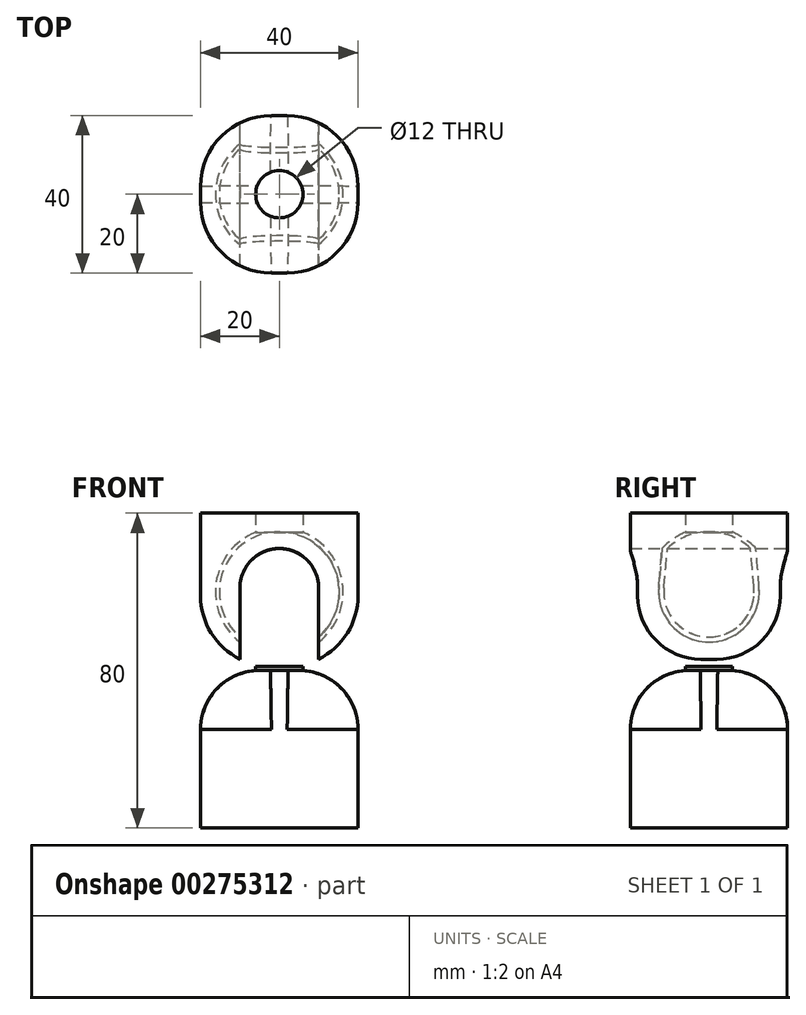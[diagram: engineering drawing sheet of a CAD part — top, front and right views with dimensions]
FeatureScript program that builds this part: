
annotation { "Feature Type Name" : "Feature", "Feature Type Description" : "" }
export const myFeature = defineFeature(function(context is Context, id is Id, definition is map)
    precondition{}
    {
        {
            var Q0;
            Q0=qCreatedBy(makeId("Front.planeOp"),FACE);
            var sketch = newSketch(context, id + "F0", { "sketchPlane" : qUnion([Q0])});
            skLineSegment(sketch, "E0.bottom", {"start": v(20, 20) * mm, "end": v(-20, 20) * mm});
            skLineSegment(sketch, "E0.top", {"start": v(20, -20) * mm, "end": v(-20, -20) * mm});
            skLineSegment(sketch, "E0.left", {"start": v(20, 20) * mm, "end": v(20, -20) * mm});
            skLineSegment(sketch, "E0.right", {"start": v(-20, 20) * mm, "end": v(-20, -20) * mm});
            skPoint(sketch, "E0.middle", {"position": v(0, 0) * mm});
            skSolve(sketch);
        }
        {
            var Q0;
            Q0 = qSketchRegion(id + "F0", true);
            extrude(context, id + "F1", {"entities" : qUnion([Q0]), "endBound" : BoundingType.SYMMETRIC, "depth" : 40 * mm});
        }
        {
            var Q0;
            Q0=qCreatedBy(makeId("Front.planeOp"),FACE);
            var sketch = newSketch(context, id + "F2", { "sketchPlane" : qUnion([Q0])});
            skLineSegment(sketch, "E1", {"start": v(0, 0) * mm, "end": v(0, 55.23) * mm});
            skArc(sketch, "E2", {"start": v(6, 26) * mm, "mid": v(14.92, 43.06) * mm, "end": v(0, 55.23) * mm});
            skLineSegment(sketch, "E3", {"start": v(6, 26) * mm, "end": v(6, 0) * mm});
            skLineSegment(sketch, "E4", {"start": v(6, 0) * mm, "end": v(0, 0) * mm});
            skSolve(sketch);
        }
        {
            var Q0;
            Q0=makeQuery(id+"F2.imprint","IMPRINT",FACE,{"disambiguationData":[TD([[makeQuery(id+"F2.imprint","IMPRINT",EDGE,{"derivedFrom":sQuery(id+"F2.wireOp",EDGE,"E1")}),-1.0]])]});
            var Q1;
            Q1=sQuery(id+"F2.wireOp",EDGE,"E1");
            revolve(context, id + "F3", {"operationType" : NewBodyOperationType.ADD, "entities" : qUnion([Q0]), "axis" : qUnion([Q1]), "revolveType" : RevolveType.FULL});
        }
        {
            var Q0;
            Q0=makeQuery(id+"F1.opExtrude","CAP_EDGE",EDGE,{"disambiguationData":[OSD([sQuery(id+"F0.wireOp",EDGE,"E0.left")])],"isStart":false});
            var Q1;
            Q1=makeQuery(id+"F1.opExtrude","CAP_EDGE",EDGE,{"disambiguationData":[OSD([sQuery(id+"F0.wireOp",EDGE,"E0.left")])],"isStart":true});
            var Q2;
            Q2=makeQuery(id+"F1.opExtrude","CAP_EDGE",EDGE,{"disambiguationData":[OSD([sQuery(id+"F0.wireOp",EDGE,"E0.right")])],"isStart":true});
            var Q3;
            Q3=makeQuery(id+"F1.opExtrude","CAP_EDGE",EDGE,{"disambiguationData":[OSD([sQuery(id+"F0.wireOp",EDGE,"E0.right")])],"isStart":false});
            fillet(context, id + "F4", {"entities" : qUnion([Q0, Q1, Q2, Q3]), "radius" : 18 * mm, "tangentPropagation" : true, "allowEdgeOverflow" : false});
        }
        {
            var Q0;
            Q0=makeQuery(id+"F1.opExtrude","SWEPT_FACE",FACE,{"disambiguationData":[OSD([sQuery(id+"F0.wireOp",EDGE,"E0.bottom")])]});
            var sketch = newSketch(context, id + "F5", { "sketchPlane" : qUnion([Q0])});
            skLineSegment(sketch, "E5.0.0", {"start": v(20, -2) * mm, "end": v(20, 2) * mm});
            skArc(sketch, "E5.0.1", {"start": v(20, 2) * mm, "mid": v(14.73, 14.73) * mm, "end": v(2, 20) * mm});
            skLineSegment(sketch, "E5.0.2", {"start": v(2, 20) * mm, "end": v(-2, 20) * mm});
            skArc(sketch, "E5.0.3", {"start": v(-2, 20) * mm, "mid": v(-14.73, 14.73) * mm, "end": v(-20, 2) * mm});
            skLineSegment(sketch, "E5.0.4", {"start": v(-20, 2) * mm, "end": v(-20, -2) * mm});
            skArc(sketch, "E5.0.5", {"start": v(-20, -2) * mm, "mid": v(-14.73, -14.73) * mm, "end": v(-2, -20) * mm});
            skLineSegment(sketch, "E5.0.6", {"start": v(-2, -20) * mm, "end": v(2, -20) * mm});
            skArc(sketch, "E5.0.7", {"start": v(2, -20) * mm, "mid": v(14.73, -14.73) * mm, "end": v(20, -2) * mm});
            skCircle(sketch, "E6.0", {"center": v(0, 0) * mm, "radius": 6 * mm});
            skSolve(sketch);
        }
        {
            var Q0;
            Q0 = qSketchRegion(id + "F5", true);
            extrude(context, id + "F6", {"entities" : qUnion([Q0]), "depth" : 40 * mm});
        }
        {
            var Q0;
            Q0=makeQuery(id+"F1.opExtrude","SWEPT_BODY",BODY,{"disambiguationData":[OSD([sQuery(id+"F0.wireOp",EDGE,"E0.bottom"),sQuery(id+"F0.wireOp",EDGE,"E0.top"),sQuery(id+"F0.wireOp",EDGE,"E0.left"),sQuery(id+"F0.wireOp",EDGE,"E0.right")])]});
            var Q1;
            Q1=makeQuery(id+"F6.opExtrude","SWEPT_BODY",BODY,{"disambiguationData":[OSD([sQuery(id+"F5.wireOp",EDGE,"E5.0.0"),sQuery(id+"F5.wireOp",EDGE,"E5.0.1"),sQuery(id+"F5.wireOp",EDGE,"E5.0.2"),sQuery(id+"F5.wireOp",EDGE,"E5.0.3"),sQuery(id+"F5.wireOp",EDGE,"E5.0.4"),sQuery(id+"F5.wireOp",EDGE,"E5.0.5"),sQuery(id+"F5.wireOp",EDGE,"E5.0.6"),sQuery(id+"F5.wireOp",EDGE,"E5.0.7"),sQuery(id+"F5.wireOp",EDGE,"E6.0")])]});
            booleanBodies(context, id + "F7", {"operationType" : BooleanOperationType.SUBTRACTION, "tools" : qUnion([Q0]), "targets" : qUnion([Q1]), "offset" : true, "offsetAll" : true, "offsetDistance" : 1 * mm, "keepTools" : true});
        }
        {
            var Q0;
            Q0=makeQuery(id+"F6.opExtrude","SWEPT_FACE",FACE,{"disambiguationData":[OSD([sQuery(id+"F5.wireOp",EDGE,"E5.0.2")])]});
            var sketch = newSketch(context, id + "F8", { "sketchPlane" : qUnion([Q0])});
            skLineSegment(sketch, "E7", {"start": v(-10, 21) * mm, "end": v(10, 21) * mm});
            skLineSegment(sketch, "E8", {"start": v(-10, 21) * mm, "end": v(-10, 41) * mm});
            skLineSegment(sketch, "E9", {"start": v(0, 51) * mm, "end": v(0, 51) * mm});
            skLineSegment(sketch, "E10", {"start": v(10, 41) * mm, "end": v(10, 21) * mm});
            skPoint(sketch, "E11.visualSharp", {"position": v(-10, 51) * mm});
            skArc(sketch, "E11.filletArc", {"start": v(0, 51) * mm, "mid": v(-7.07, 48.07) * mm, "end": v(-10, 41) * mm});
            skPoint(sketch, "E12.visualSharp", {"position": v(10, 51) * mm});
            skArc(sketch, "E12.filletArc", {"start": v(10, 41) * mm, "mid": v(7.07, 48.07) * mm, "end": v(0, 51) * mm});
            skSolve(sketch);
        }
        {
            var Q0;
            Q0 = qSketchRegion(id + "F8", true);
            extrude(context, id + "F9", {"entities" : qUnion([Q0]), "operationType" : NewBodyOperationType.REMOVE, "endBound" : BoundingType.THROUGH_ALL, "oppositeDirection" : true, "depth" : 25 * mm});
        }
        {
            var Q0;
            Q0=makeQuery(id+"F7.tempBoolean.opBoolean","INTERSECT",EDGE,{"derivedFrom":[makeQuery(id+"F6.opExtrude","SWEPT_FACE",FACE,{"disambiguationData":[OSD([sQuery(id+"F5.wireOp",EDGE,"E5.0.7")])]}),makeQuery(id+"F7.offsetTempBody.opPattern","COPY",FACE,{"derivedFrom":makeQuery(id+"F1.opExtrude","SWEPT_FACE",FACE,{"disambiguationData":[OSD([sQuery(id+"F0.wireOp",EDGE,"E0.bottom")])]}),"instanceName":"1"})]});
            var Q1;
            Q1=makeQuery(id+"F7.tempBoolean.opBoolean","INTERSECT",EDGE,{"derivedFrom":[makeQuery(id+"F6.opExtrude","SWEPT_FACE",FACE,{"disambiguationData":[OSD([sQuery(id+"F5.wireOp",EDGE,"E5.0.5")])]}),makeQuery(id+"F7.offsetTempBody.opPattern","COPY",FACE,{"derivedFrom":makeQuery(id+"F1.opExtrude","SWEPT_FACE",FACE,{"disambiguationData":[OSD([sQuery(id+"F0.wireOp",EDGE,"E0.bottom")])]}),"instanceName":"1"})]});
            fillet(context, id + "F10", {"entities" : qUnion([Q0, Q1]), "radius" : 18 * mm, "tangentPropagation" : true, "allowEdgeOverflow" : false});
        }
        {
            var Q0;
            Q0=makeQuery(id+"F4.opFillet","BLEND_EDGE",EDGE,{"blendedFrom":[makeQuery(id+"F1.opExtrude","CAP_EDGE",EDGE,{"disambiguationData":[OSD([sQuery(id+"F0.wireOp",EDGE,"E0.right")])],"isStart":true}),makeQuery(id+"F1.opExtrude","SWEPT_FACE",FACE,{"disambiguationData":[OSD([sQuery(id+"F0.wireOp",EDGE,"E0.bottom")])]})],"blendedInto":[makeQuery(id+"F1.opExtrude","SWEPT_FACE",FACE,{"disambiguationData":[OSD([sQuery(id+"F0.wireOp",EDGE,"E0.bottom")])]})]});
            fillet(context, id + "F11", {"entities" : qUnion([Q0]), "radius" : 15 * mm, "tangentPropagation" : true, "allowEdgeOverflow" : false});
        }
    });
